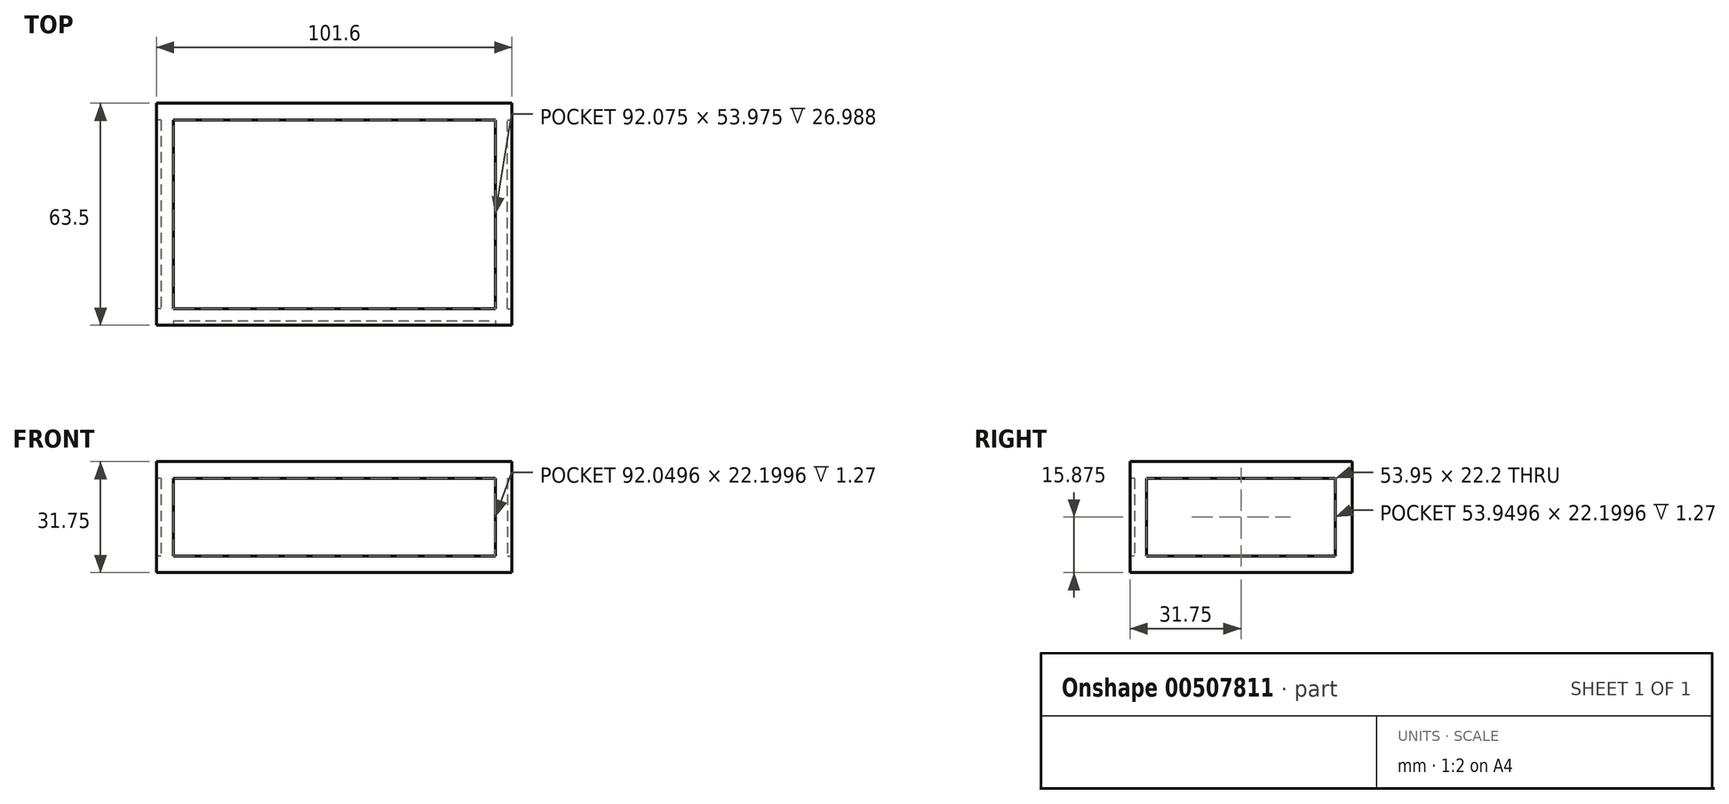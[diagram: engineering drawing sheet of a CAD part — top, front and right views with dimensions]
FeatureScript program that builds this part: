
annotation { "Feature Type Name" : "Feature", "Feature Type Description" : "" }
export const myFeature = defineFeature(function(context is Context, id is Id, definition is map)
    precondition{}
    {
        {
            var Q0;
            Q0=qCreatedBy(makeId("Top.planeOp"),FACE);
            var sketch = newSketch(context, id + "F0", { "sketchPlane" : qUnion([Q0])});
            skLineSegment(sketch, "E0.bottom", {"start": v(-50.8, 31.75) * mm, "end": v(50.8, 31.75) * mm});
            skLineSegment(sketch, "E0.top", {"start": v(-50.8, -31.75) * mm, "end": v(50.8, -31.75) * mm});
            skLineSegment(sketch, "E0.left", {"start": v(-50.8, 31.75) * mm, "end": v(-50.8, -31.75) * mm});
            skLineSegment(sketch, "E0.right", {"start": v(50.8, 31.75) * mm, "end": v(50.8, -31.75) * mm});
            skSolve(sketch);
        }
        {
            var Q0;
            Q0=makeQuery(id+"F0.imprint","IMPRINT",FACE,{"disambiguationData":[TD([[makeQuery(id+"F0.imprint","IMPRINT",EDGE,{"derivedFrom":sQuery(id+"F0.wireOp",EDGE,"E0.bottom")}),-1.0]])]});
            extrude(context, id + "F1", {"entities" : qUnion([Q0]), "depth" : 31.75 * mm});
        }
        {
            var Q0;
            Q0=makeQuery(id+"F1.opExtrude","CAP_FACE",FACE,{"disambiguationData":[OSD([sQuery(id+"F0.wireOp",EDGE,"E0.bottom"),sQuery(id+"F0.wireOp",EDGE,"E0.top"),sQuery(id+"F0.wireOp",EDGE,"E0.left"),sQuery(id+"F0.wireOp",EDGE,"E0.right")])],"isStart":false});
            shell(context, id + "F2", {"entities" : qUnion([Q0]), "thickness" : 4.76 * mm});
        }
        {
            var Q0;
            Q0=makeQuery(id+"F1.opExtrude","SWEPT_FACE",FACE,{"disambiguationData":[OSD([sQuery(id+"F0.wireOp",EDGE,"E0.top")])]});
            var sketch = newSketch(context, id + "F3", { "sketchPlane" : qUnion([Q0])});
            skLineSegment(sketch, "E1.bottom", {"start": v(-46.02, 26.97) * mm, "end": v(46.02, 26.97) * mm});
            skLineSegment(sketch, "E1.top", {"start": v(-46.02, 4.78) * mm, "end": v(46.02, 4.78) * mm});
            skLineSegment(sketch, "E1.left", {"start": v(-46.02, 26.97) * mm, "end": v(-46.02, 4.78) * mm});
            skLineSegment(sketch, "E1.right", {"start": v(46.02, 26.97) * mm, "end": v(46.02, 4.78) * mm});
            skSolve(sketch);
        }
        {
            var Q0;
            Q0=makeQuery(id+"F1.opExtrude","SWEPT_FACE",FACE,{"disambiguationData":[OSD([sQuery(id+"F0.wireOp",EDGE,"E0.left")])]});
            var sketch = newSketch(context, id + "F4", { "sketchPlane" : qUnion([Q0])});
            skLineSegment(sketch, "E2.bottom", {"start": v(-26.97, 26.97) * mm, "end": v(26.97, 26.97) * mm});
            skLineSegment(sketch, "E2.top", {"start": v(-26.97, 4.78) * mm, "end": v(26.97, 4.78) * mm});
            skLineSegment(sketch, "E2.left", {"start": v(-26.97, 26.97) * mm, "end": v(-26.97, 4.78) * mm});
            skLineSegment(sketch, "E2.right", {"start": v(26.97, 26.97) * mm, "end": v(26.97, 4.78) * mm});
            skSolve(sketch);
        }
        {
            var Q0;
            Q0=makeQuery(id+"F1.opExtrude","SWEPT_FACE",FACE,{"disambiguationData":[OSD([sQuery(id+"F0.wireOp",EDGE,"E0.right")])]});
            var sketch = newSketch(context, id + "F5", { "sketchPlane" : qUnion([Q0])});
            skLineSegment(sketch, "E3.bottom", {"start": v(-26.97, 26.97) * mm, "end": v(26.97, 26.97) * mm});
            skLineSegment(sketch, "E3.top", {"start": v(-26.97, 4.78) * mm, "end": v(26.97, 4.78) * mm});
            skLineSegment(sketch, "E3.left", {"start": v(-26.97, 26.97) * mm, "end": v(-26.97, 4.78) * mm});
            skLineSegment(sketch, "E3.right", {"start": v(26.97, 26.97) * mm, "end": v(26.97, 4.78) * mm});
            skSolve(sketch);
        }
        {
            var Q0;
            Q0=makeQuery(id+"F4.imprint","IMPRINT",FACE,{"disambiguationData":[TD([[makeQuery(id+"F4.imprint","IMPRINT",EDGE,{"derivedFrom":sQuery(id+"F4.wireOp",EDGE,"E2.bottom")}),-1.0]])]});
            extrude(context, id + "F6", {"entities" : qUnion([Q0]), "operationType" : NewBodyOperationType.REMOVE, "oppositeDirection" : true, "depth" : 1.27 * mm});
        }
        {
            var Q0;
            Q0=makeQuery(id+"F3.imprint","IMPRINT",FACE,{"disambiguationData":[TD([[makeQuery(id+"F3.imprint","IMPRINT",EDGE,{"derivedFrom":sQuery(id+"F3.wireOp",EDGE,"E1.bottom")}),-1.0]])]});
            extrude(context, id + "F7", {"entities" : qUnion([Q0]), "operationType" : NewBodyOperationType.REMOVE, "oppositeDirection" : true, "depth" : 1.27 * mm});
        }
        {
            var Q0;
            Q0=makeQuery(id+"F5.imprint","IMPRINT",FACE,{"disambiguationData":[TD([[makeQuery(id+"F5.imprint","IMPRINT",EDGE,{"derivedFrom":sQuery(id+"F5.wireOp",EDGE,"E3.bottom")}),-1.0]])]});
            extrude(context, id + "F8", {"entities" : qUnion([Q0]), "operationType" : NewBodyOperationType.REMOVE, "oppositeDirection" : true, "depth" : 1.27 * mm});
        }
    });
